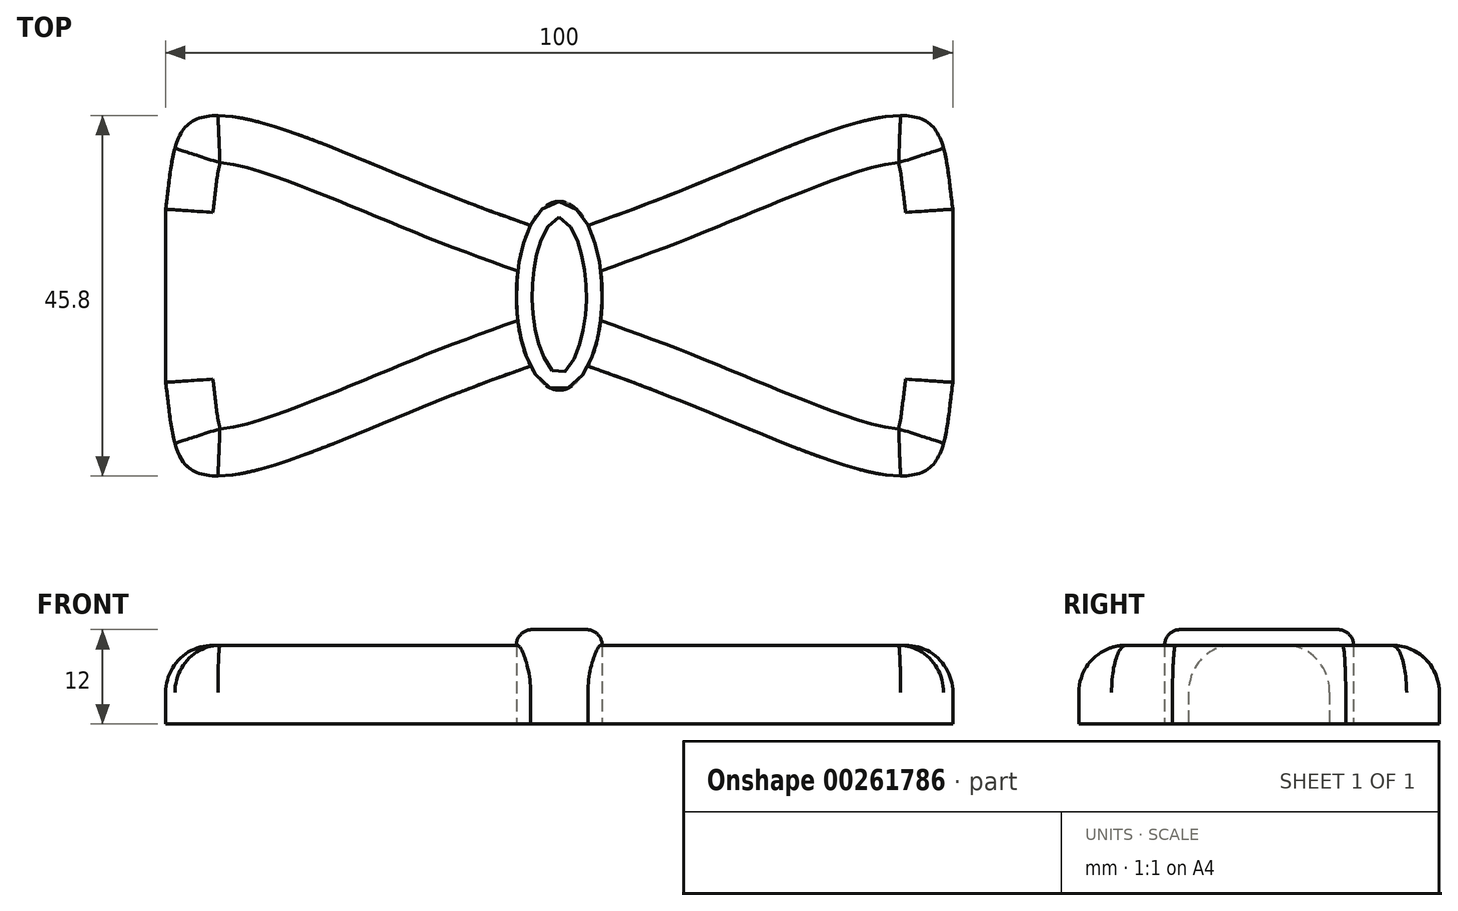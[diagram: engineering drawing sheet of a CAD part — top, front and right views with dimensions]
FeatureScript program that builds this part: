
annotation { "Feature Type Name" : "Feature", "Feature Type Description" : "" }
export const myFeature = defineFeature(function(context is Context, id is Id, definition is map)
    precondition{}
    {
        {
            var Q0;
            Q0=qCreatedBy(makeId("Top.planeOp"),FACE);
            var sketch = newSketch(context, id + "F0", { "sketchPlane" : qUnion([Q0])});
            skLineSegment(sketch, "E0", {"start": v(0, 0) * mm, "end": v(0, 12) * mm});
            skLineSegment(sketch, "E1", {"start": v(0, 0) * mm, "end": v(0, -12) * mm});
            skLineSegment(sketch, "E2", {"start": v(0, 0) * mm, "end": v(-50, 0) * mm});
            skLineSegment(sketch, "E3", {"start": v(0, 0) * mm, "end": v(50, 0) * mm});
            skLineSegment(sketch, "E4", {"start": v(-50, 0) * mm, "end": v(-50, 22) * mm});
            skLineSegment(sketch, "E5", {"start": v(-50, 0) * mm, "end": v(-50, -22) * mm});
            skLineSegment(sketch, "E6", {"start": v(50, 0) * mm, "end": v(50, 22) * mm});
            skLineSegment(sketch, "E7", {"start": v(50, 0) * mm, "end": v(50, -22) * mm});
            skEllipse(sketch, "E8", {"center": v(0, 0) * mm, "majorRadius": 12 * mm, "minorRadius": 5.45 * mm, "majorAxis": v(0, 1)});
            skFitSpline(sketch, "E9", {"points": [v(-3.63, 8.95) * mm, v(-36.87, 21.7) * mm, v(-47.22, 21.7) * mm, v(-50, 11) * mm], "startDerivative": vector(-84.06, 28.4) * mm, "endDerivative": vector(-7.14, -51.83) * mm});
            skFitSpline(sketch, "E10.MirrorCS", {"points": [v(-3.63, -8.95) * mm, v(-36.87, -21.7) * mm, v(-47.22, -21.7) * mm, v(-50, -11) * mm], "startDerivative": vector(-84.06, -28.4) * mm, "endDerivative": vector(-7.14, 51.83) * mm});
            skFitSpline(sketch, "E11.MirrorCS", {"points": [v(3.63, 8.95) * mm, v(36.87, 21.7) * mm, v(47.22, 21.7) * mm, v(50, 11) * mm], "startDerivative": vector(84.06, 28.4) * mm, "endDerivative": vector(7.14, -51.83) * mm});
            skFitSpline(sketch, "E12.MirrorCS", {"points": [v(3.63, -8.95) * mm, v(36.87, -21.7) * mm, v(47.22, -21.7) * mm, v(50, -11) * mm], "startDerivative": vector(84.06, -28.4) * mm, "endDerivative": vector(7.14, 51.83) * mm});
            skSolve(sketch);
        }
        {
            var Q0;
            {var subQ5=sQuery(id+"F0.wireOp",EDGE,"E9");Q0=makeQuery(id+"F0.imprint","IMPRINT",FACE,{"disambiguationData":[TD([[makeQuery(id+"F0.imprint","IMPRINT",EDGE,{"derivedFrom":subQ5}),1.0]])]});}
            var Q1;
            {var subQ5=sQuery(id+"F0.wireOp",EDGE,"E10.MirrorCS");Q1=makeQuery(id+"F0.imprint","IMPRINT",FACE,{"disambiguationData":[TD([[makeQuery(id+"F0.imprint","IMPRINT",EDGE,{"derivedFrom":subQ5}),-1.0]])]});}
            var Q2;
            {var subQ5=sQuery(id+"F0.wireOp",EDGE,"E11.MirrorCS");Q2=makeQuery(id+"F0.imprint","IMPRINT",FACE,{"disambiguationData":[TD([[makeQuery(id+"F0.imprint","IMPRINT",EDGE,{"derivedFrom":subQ5}),-1.0]])]});}
            var Q3;
            {var subQ5=sQuery(id+"F0.wireOp",EDGE,"E12.MirrorCS");Q3=makeQuery(id+"F0.imprint","IMPRINT",FACE,{"disambiguationData":[TD([[makeQuery(id+"F0.imprint","IMPRINT",EDGE,{"derivedFrom":subQ5}),1.0]])]});}
            extrude(context, id + "F1", {"entities" : qUnion([Q0, Q1, Q2, Q3]), "depth" : 10 * mm});
        }
        {
            var Q0;
            {var subQ0=sQuery(id+"F0.wireOp",EDGE,"E0");Q0=makeQuery(id+"F0.imprint","IMPRINT",FACE,{"disambiguationData":[TD([[makeQuery(id+"F0.imprint","IMPRINT",EDGE,{"derivedFrom":subQ0}),-1.0]])]});}
            var Q1;
            {var subQ0=sQuery(id+"F0.wireOp",EDGE,"E0");Q1=makeQuery(id+"F0.imprint","IMPRINT",FACE,{"disambiguationData":[TD([[makeQuery(id+"F0.imprint","IMPRINT",EDGE,{"derivedFrom":subQ0}),1.0]])]});}
            var Q2;
            {var subQ0=sQuery(id+"F0.wireOp",EDGE,"E1");Q2=makeQuery(id+"F0.imprint","IMPRINT",FACE,{"disambiguationData":[TD([[makeQuery(id+"F0.imprint","IMPRINT",EDGE,{"derivedFrom":subQ0}),-1.0]])]});}
            var Q3;
            {var subQ0=sQuery(id+"F0.wireOp",EDGE,"E1");Q3=makeQuery(id+"F0.imprint","IMPRINT",FACE,{"disambiguationData":[TD([[makeQuery(id+"F0.imprint","IMPRINT",EDGE,{"derivedFrom":subQ0}),1.0]])]});}
            extrude(context, id + "F2", {"entities" : qUnion([Q0, Q1, Q2, Q3]), "depth" : 12 * mm});
        }
        {
            var Q0;
            Q0=makeQuery(id+"F1.opExtrude","CAP_EDGE",EDGE,{"disambiguationData":[OSD([sQuery(id+"F0.wireOp",EDGE,"E10.MirrorCS")])],"isStart":false});
            var Q1;
            Q1=makeQuery(id+"F1.opExtrude","CAP_EDGE",EDGE,{"disambiguationData":[OSD([sQuery(id+"F0.wireOp",EDGE,"E9")])],"isStart":false});
            var Q2;
            Q2=makeQuery(id+"F1.opExtrude","CAP_EDGE",EDGE,{"disambiguationData":[OSD([sQuery(id+"F0.wireOp",EDGE,"E11.MirrorCS")])],"isStart":false});
            var Q3;
            Q3=makeQuery(id+"F1.opExtrude","CAP_EDGE",EDGE,{"disambiguationData":[OSD([sQuery(id+"F0.wireOp",EDGE,"E12.MirrorCS")])],"isStart":false});
            var Q4;
            Q4=makeQuery(id+"F1.opExtrude","CAP_EDGE",EDGE,{"disambiguationData":[OSD([sQuery(id+"F0.wireOp",EDGE,"E6"),sQuery(id+"F0.wireOp",EDGE,"E7")])],"isStart":false});
            var Q5;
            Q5=makeQuery(id+"F1.opExtrude","CAP_EDGE",EDGE,{"disambiguationData":[OSD([sQuery(id+"F0.wireOp",EDGE,"E4"),sQuery(id+"F0.wireOp",EDGE,"E5")])],"isStart":false});
            fillet(context, id + "F3", {"entities" : qUnion([Q0, Q1, Q2, Q3, Q4, Q5]), "radius" : 6 * mm, "tangentPropagation" : true, "allowEdgeOverflow" : false});
        }
        {
            var Q0;
            Q0=makeQuery(id+"F2.opExtrude","CAP_EDGE",EDGE,{"disambiguationData":[OSD([sQuery(id+"F0.wireOp",EDGE,"E8")])],"isStart":false});
            fillet(context, id + "F4", {"entities" : qUnion([Q0]), "radius" : 2 * mm, "tangentPropagation" : true, "allowEdgeOverflow" : false});
        }
    });
